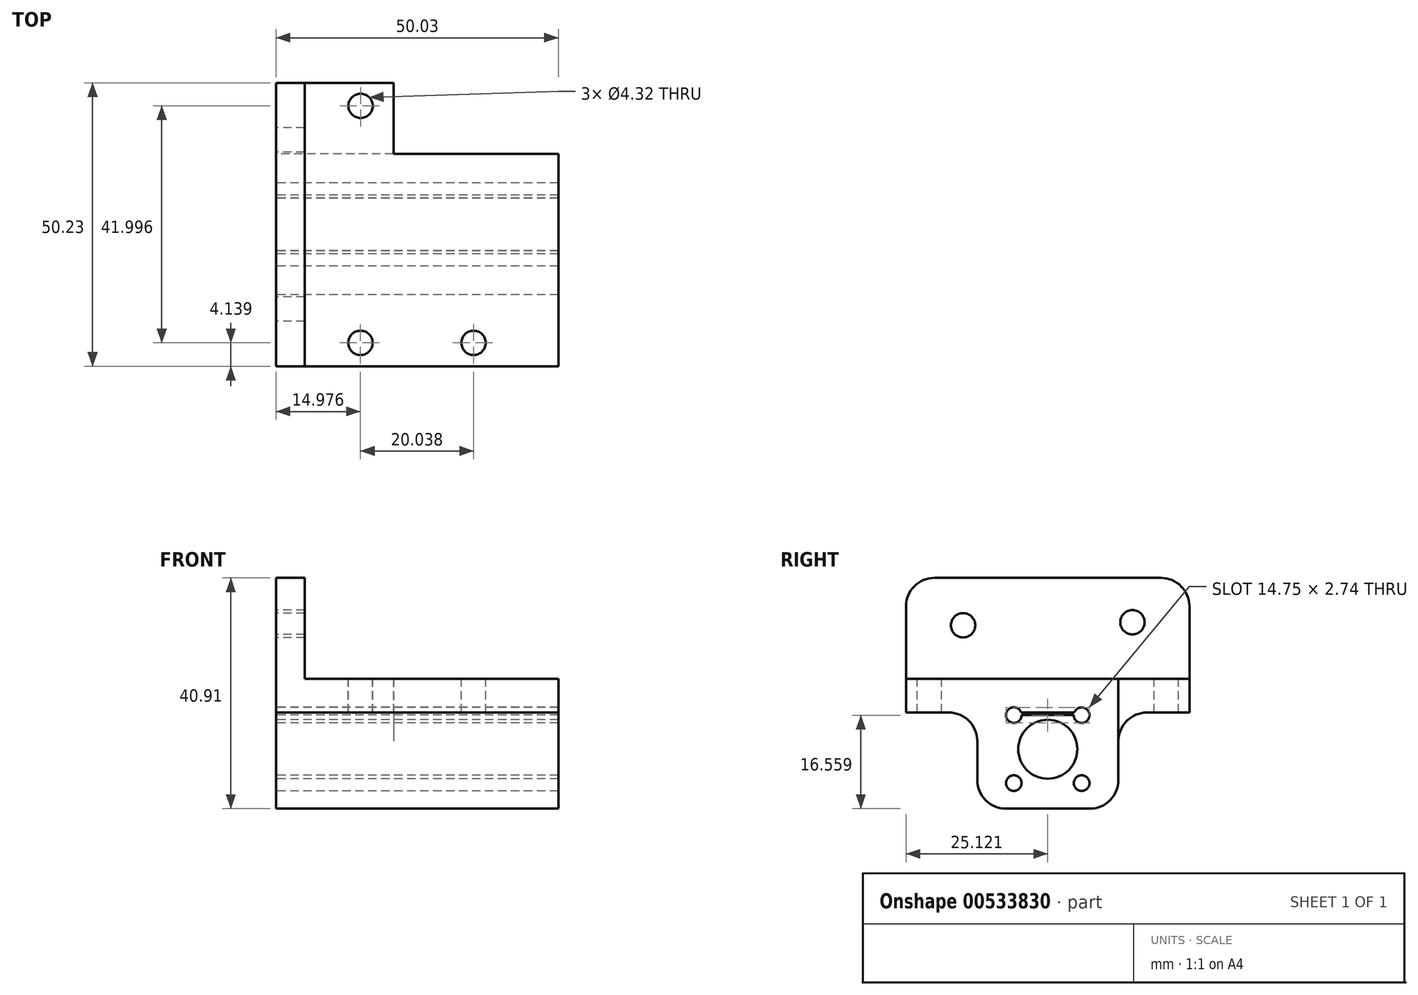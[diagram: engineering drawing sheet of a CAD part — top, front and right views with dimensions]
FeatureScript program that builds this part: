
annotation { "Feature Type Name" : "Feature", "Feature Type Description" : "" }
export const myFeature = defineFeature(function(context is Context, id is Id, definition is map)
    precondition{}
    {
        {
            var Q0;
            Q0=qCreatedBy(makeId("Right.planeOp"),FACE);
            cPlane(context, id + "F0", {"entities" : qUnion([Q0]), "cplaneType" : CPlaneType.OFFSET, "offset" : 25 * mm, "oppositeDirection" : true, "width" : 152.4 * mm, "height" : 152.4 * mm});
        }
        {
            var Q0;
            Q0=qCreatedBy(id+"F0.planeOp",FACE);
            var sketch = newSketch(context, id + "F1", { "sketchPlane" : qUnion([Q0])});
            skLineSegment(sketch, "E0.bottom", {"start": v(25.1, -3.49) * mm, "end": v(-25.13, -3.49) * mm});
            skLineSegment(sketch, "E0.top", {"start": v(25.1, 20.38) * mm, "end": v(-25.13, 20.38) * mm});
            skLineSegment(sketch, "E0.left", {"start": v(25.1, -3.49) * mm, "end": v(25.1, 20.38) * mm});
            skLineSegment(sketch, "E0.right", {"start": v(-25.13, -3.49) * mm, "end": v(-25.13, 20.38) * mm});
            skLineSegment(sketch, "E1.bottom", {"start": v(12.51, -3.49) * mm, "end": v(-12.48, -3.49) * mm});
            skLineSegment(sketch, "E1.top", {"start": v(12.51, -20.53) * mm, "end": v(-12.48, -20.53) * mm});
            skLineSegment(sketch, "E1.left", {"start": v(12.51, -3.49) * mm, "end": v(12.51, -20.53) * mm});
            skLineSegment(sketch, "E1.right", {"start": v(-12.48, -3.49) * mm, "end": v(-12.48, -20.53) * mm});
            skCircle(sketch, "E2", {"center": v(15, 12.5) * mm, "radius": 2 * mm});
            skCircle(sketch, "E3", {"center": v(-15, 11.97) * mm, "radius": 2 * mm});
            skCircle(sketch, "E4", {"center": v(0, -10) * mm, "radius": 5.23 * mm});
            skCircle(sketch, "E5", {"center": v(-6.02, -3.94) * mm, "radius": 1.39 * mm});
            skCircle(sketch, "E6", {"center": v(6, -3.96) * mm, "radius": 1.39 * mm});
            skLineSegment(sketch, "E7.bottom", {"start": v(6, -3.96) * mm, "end": v(-6.01, -3.96) * mm});
            skLineSegment(sketch, "E7.top", {"start": v(6, -16) * mm, "end": v(-6.01, -16) * mm});
            skLineSegment(sketch, "E7.left", {"start": v(6, -3.96) * mm, "end": v(6, -16) * mm});
            skLineSegment(sketch, "E7.right", {"start": v(-6.01, -3.96) * mm, "end": v(-6.01, -16) * mm});
            skCircle(sketch, "E8", {"center": v(6, -16) * mm, "radius": 1.39 * mm});
            skCircle(sketch, "E9", {"center": v(-6.01, -16) * mm, "radius": 1.39 * mm});
            skSolve(sketch);
        }
        {
            var Q0;
            {var subQ0=sQuery(id+"F1.wireOp",EDGE,"E6");var subQ1=sQuery(id+"F1.wireOp",EDGE,"E1.bottom");var subQ2=makeQuery(id+"F1.imprint","INTERSECT",VERTEX,{"disambiguationData":[OD(1.0)],"derivedFrom":[subQ1,subQ0]});Q0=makeQuery(id+"F1.imprint","IMPRINT",FACE,{"disambiguationData":[TD([[makeQuery(id+"F1.imprint","IMPRINT",EDGE,{"disambiguationData":[TD([[subQ2,-1.0]])],"derivedFrom":subQ1}),1.0]])]});}
            var Q1;
            Q1=makeQuery(id+"F1.imprint","IMPRINT",FACE,{"disambiguationData":[TD([[makeQuery(id+"F1.imprint","IMPRINT",EDGE,{"derivedFrom":sQuery(id+"F1.wireOp",EDGE,"E4")}),-1.0]])]});
            var Q2;
            Q2=makeQuery(id+"F1.imprint","IMPRINT",FACE,{"disambiguationData":[TD([[makeQuery(id+"F1.imprint","IMPRINT",EDGE,{"derivedFrom":sQuery(id+"F1.wireOp",EDGE,"E0.top")}),1.0]])]});
            var Q3;
            Q3=makeQuery(id+"F1.imprint","IMPRINT",FACE,{"disambiguationData":[TD([[makeQuery(id+"F1.imprint","IMPRINT",EDGE,{"derivedFrom":sQuery(id+"F1.wireOp",EDGE,"E1.top")}),-1.0]])]});
            extrude(context, id + "F2", {"entities" : qUnion([Q0, Q1, Q2, Q3]), "depth" : 5.08 * mm, "offsetDistance" : 25.4 * mm});
        }
        {
            var Q0;
            Q0=makeQuery(id+"F2.opExtrude","CAP_FACE",FACE,{"disambiguationData":[OSD([sQuery(id+"F1.wireOp",EDGE,"E0.bottom"),sQuery(id+"F1.wireOp",EDGE,"E0.top"),sQuery(id+"F1.wireOp",EDGE,"E0.left"),sQuery(id+"F1.wireOp",EDGE,"E0.right"),sQuery(id+"F1.wireOp",EDGE,"E1.top"),sQuery(id+"F1.wireOp",EDGE,"E1.left"),sQuery(id+"F1.wireOp",EDGE,"E1.right"),sQuery(id+"F1.wireOp",EDGE,"E2"),sQuery(id+"F1.wireOp",EDGE,"E3"),sQuery(id+"F1.wireOp",EDGE,"E4"),sQuery(id+"F1.wireOp",EDGE,"E5"),sQuery(id+"F1.wireOp",EDGE,"E6"),sQuery(id+"F1.wireOp",EDGE,"E8"),sQuery(id+"F1.wireOp",EDGE,"E9")])],"isStart":false});
            var sketch = newSketch(context, id + "F3", { "sketchPlane" : qUnion([Q0])});
            skLineSegment(sketch, "E10", {"start": v(-25.13, 2.5) * mm, "end": v(25.1, 2.5) * mm});
            skSolve(sketch);
        }
        {
            var Q0;
            {var subQ2=sQuery(id+"F3.wireOp",EDGE,"E10");Q0=makeQuery(id+"F3.imprint","IMPRINT",FACE,{"disambiguationData":[TD([[makeQuery(id+"F3.imprint","IMPRINT",EDGE,{"derivedFrom":subQ2}),-1.0]])]});}
            extrude(context, id + "F4", {"entities" : qUnion([Q0]), "operationType" : NewBodyOperationType.ADD, "depth" : 15.75 * mm, "offsetDistance" : 25.4 * mm});
        }
        {
            var Q0;
            Q0=makeQuery(id+"F4.opExtrude","CAP_FACE",FACE,{"disambiguationData":[OSD([sQuery(id+"F1.wireOp",EDGE,"E0.bottom"),sQuery(id+"F1.wireOp",EDGE,"E0.left"),sQuery(id+"F1.wireOp",EDGE,"E0.right"),sQuery(id+"F1.wireOp",EDGE,"E1.top"),sQuery(id+"F1.wireOp",EDGE,"E1.left"),sQuery(id+"F1.wireOp",EDGE,"E1.right"),sQuery(id+"F1.wireOp",EDGE,"E4"),sQuery(id+"F1.wireOp",EDGE,"E5"),sQuery(id+"F1.wireOp",EDGE,"E6"),sQuery(id+"F1.wireOp",EDGE,"E8"),sQuery(id+"F1.wireOp",EDGE,"E9"),sQuery(id+"F3.wireOp",EDGE,"E10")])],"isStart":false});
            var sketch = newSketch(context, id + "F5", { "sketchPlane" : qUnion([Q0])});
            skLineSegment(sketch, "E11", {"start": v(12.51, -3.49) * mm, "end": v(12.51, 2.5) * mm});
            skSolve(sketch);
        }
        {
            var Q0;
            {var subQ1=sQuery(id+"F5.wireOp",EDGE,"E11");Q0=makeQuery(id+"F5.imprint","IMPRINT",FACE,{"disambiguationData":[TD([[makeQuery(id+"F5.imprint","IMPRINT",EDGE,{"derivedFrom":subQ1}),1.0]])]});}
            extrude(context, id + "F6", {"entities" : qUnion([Q0]), "operationType" : NewBodyOperationType.ADD, "depth" : 29.2 * mm, "offsetDistance" : 25.4 * mm});
        }
        {
            var Q0;
            {var subQ0=sQuery(id+"F3.wireOp",EDGE,"E10");Q0=makeQuery(id+"F6.boolean.opBoolean","MERGE",FACE,{"derivedFrom":[makeQuery(id+"F4.opExtrude","SWEPT_FACE",FACE,{"disambiguationData":[OSD([subQ0])]}),makeQuery(id+"F6.opExtrude","SWEPT_FACE",FACE,{"disambiguationData":[OSD([subQ0])]})]});}
            var sketch = newSketch(context, id + "F7", { "sketchPlane" : qUnion([Q0])});
            skCircle(sketch, "E12", {"center": v(-10, 21) * mm, "radius": 2.01 * mm});
            skCircle(sketch, "E13", {"center": v(-10.01, -20.99) * mm, "radius": 2.01 * mm});
            skCircle(sketch, "E14", {"center": v(10.02, -21) * mm, "radius": 2.01 * mm});
            skSolve(sketch);
        }
        {
            var Q0;
            Q0 = qSketchRegion(id + "F7", true);
            extrude(context, id + "F8", {"entities" : qUnion([Q0]), "operationType" : NewBodyOperationType.REMOVE, "oppositeDirection" : true, "depth" : 25.4 * mm, "offsetDistance" : 25.4 * mm});
        }
        {
            var Q0;
            {var subQ0=sQuery(id+"F1.wireOp",EDGE,"E1.right");var subQ1=sQuery(id+"F1.wireOp",EDGE,"E1.top");Q0=makeQuery(id+"F6.boolean.opBoolean","MERGE",EDGE,{"derivedFrom":[makeQuery(id+"F4.boolean.opBoolean","MERGE",EDGE,{"derivedFrom":[makeQuery(id+"F2.opExtrude","SWEPT_EDGE",EDGE,{"disambiguationData":[OSD([subQ1,subQ0])]}),makeQuery(id+"F4.opExtrude","SWEPT_EDGE",EDGE,{"disambiguationData":[OSD([subQ1,subQ0])]})]}),makeQuery(id+"F6.opExtrude","SWEPT_EDGE",EDGE,{"disambiguationData":[OSD([subQ1,subQ0])]})]});}
            var Q1;
            {var subQ0=sQuery(id+"F1.wireOp",EDGE,"E1.left");var subQ1=sQuery(id+"F1.wireOp",EDGE,"E1.top");Q1=makeQuery(id+"F6.boolean.opBoolean","MERGE",EDGE,{"derivedFrom":[makeQuery(id+"F4.boolean.opBoolean","MERGE",EDGE,{"derivedFrom":[makeQuery(id+"F2.opExtrude","SWEPT_EDGE",EDGE,{"disambiguationData":[OSD([subQ1,subQ0])]}),makeQuery(id+"F4.opExtrude","SWEPT_EDGE",EDGE,{"disambiguationData":[OSD([subQ1,subQ0])]})]}),makeQuery(id+"F6.opExtrude","SWEPT_EDGE",EDGE,{"disambiguationData":[OSD([subQ1,subQ0])]})]});}
            var Q2;
            {var subQ0=sQuery(id+"F1.wireOp",EDGE,"E1.right");var subQ1=sQuery(id+"F1.wireOp",EDGE,"E0.bottom");Q2=makeQuery(id+"F6.boolean.opBoolean","MERGE",EDGE,{"derivedFrom":[makeQuery(id+"F4.boolean.opBoolean","MERGE",EDGE,{"derivedFrom":[makeQuery(id+"F2.opExtrude","SWEPT_EDGE",EDGE,{"disambiguationData":[OSD([subQ1,sQuery(id+"F1.wireOp",EDGE,"E1.bottom"),subQ0])]}),makeQuery(id+"F4.opExtrude","SWEPT_EDGE",EDGE,{"disambiguationData":[OSD([subQ1,subQ0])]})]}),makeQuery(id+"F6.opExtrude","SWEPT_EDGE",EDGE,{"disambiguationData":[OSD([subQ1,subQ0])]})]});}
            var Q3;
            {var subQ0=sQuery(id+"F1.wireOp",EDGE,"E1.left");var subQ1=sQuery(id+"F1.wireOp",EDGE,"E0.bottom");Q3=makeQuery(id+"F4.boolean.opBoolean","MERGE",EDGE,{"derivedFrom":[makeQuery(id+"F2.opExtrude","SWEPT_EDGE",EDGE,{"disambiguationData":[OSD([subQ1,sQuery(id+"F1.wireOp",EDGE,"E1.bottom"),subQ0])]}),makeQuery(id+"F4.opExtrude","SWEPT_EDGE",EDGE,{"disambiguationData":[OSD([subQ1,subQ0])]})]});}
            var Q4;
            Q4=makeQuery(id+"F2.opExtrude","SWEPT_EDGE",EDGE,{"disambiguationData":[OSD([sQuery(id+"F1.wireOp",EDGE,"E0.top"),sQuery(id+"F1.wireOp",EDGE,"E0.right")])]});
            var Q5;
            Q5=makeQuery(id+"F2.opExtrude","SWEPT_EDGE",EDGE,{"disambiguationData":[OSD([sQuery(id+"F1.wireOp",EDGE,"E0.top"),sQuery(id+"F1.wireOp",EDGE,"E0.left")])]});
            fillet(context, id + "F9", {"entities" : qUnion([Q0, Q1, Q2, Q3, Q4, Q5]), "radius" : 5.08 * mm, "tangentPropagation" : true, "allowEdgeOverflow" : false});
        }
        {
            var Q0;
            Q0=makeQuery(id+"F2.opExtrude","CAP_FACE",FACE,{"disambiguationData":[OSD([sQuery(id+"F1.wireOp",EDGE,"E0.bottom"),sQuery(id+"F1.wireOp",EDGE,"E0.top"),sQuery(id+"F1.wireOp",EDGE,"E0.left"),sQuery(id+"F1.wireOp",EDGE,"E0.right"),sQuery(id+"F1.wireOp",EDGE,"E1.top"),sQuery(id+"F1.wireOp",EDGE,"E1.left"),sQuery(id+"F1.wireOp",EDGE,"E1.right"),sQuery(id+"F1.wireOp",EDGE,"E2"),sQuery(id+"F1.wireOp",EDGE,"E3"),sQuery(id+"F1.wireOp",EDGE,"E4"),sQuery(id+"F1.wireOp",EDGE,"E5"),sQuery(id+"F1.wireOp",EDGE,"E6"),sQuery(id+"F1.wireOp",EDGE,"E8"),sQuery(id+"F1.wireOp",EDGE,"E9")])],"isStart":true});
            var sketch = newSketch(context, id + "F10", { "sketchPlane" : qUnion([Q0])});
            skCircle(sketch, "E15", {"center": v(-15, 12.5) * mm, "radius": 2.16 * mm});
            skCircle(sketch, "E16", {"center": v(15, 11.97) * mm, "radius": 2.16 * mm});
            skSolve(sketch);
        }
        {
            var Q0;
            Q0 = qSketchRegion(id + "F10", true);
            extrude(context, id + "F11", {"entities" : qUnion([Q0]), "operationType" : NewBodyOperationType.REMOVE, "oppositeDirection" : true, "depth" : 25.4 * mm, "offsetDistance" : 25.4 * mm});
        }
        {
            var Q0;
            {var subQ0=sQuery(id+"F3.wireOp",EDGE,"E10");Q0=makeQuery(id+"F6.boolean.opBoolean","MERGE",FACE,{"derivedFrom":[makeQuery(id+"F4.opExtrude","SWEPT_FACE",FACE,{"disambiguationData":[OSD([subQ0])]}),makeQuery(id+"F6.opExtrude","SWEPT_FACE",FACE,{"disambiguationData":[OSD([subQ0])]})]});}
            var sketch = newSketch(context, id + "F12", { "sketchPlane" : qUnion([Q0])});
            skCircle(sketch, "E17", {"center": v(-10, 21) * mm, "radius": 2.16 * mm});
            skCircle(sketch, "E18", {"center": v(-10.01, -20.99) * mm, "radius": 2.16 * mm});
            skCircle(sketch, "E19", {"center": v(10.02, -21) * mm, "radius": 2.16 * mm});
            skSolve(sketch);
        }
        {
            var Q0;
            Q0 = qSketchRegion(id + "F12", true);
            extrude(context, id + "F13", {"entities" : qUnion([Q0]), "operationType" : NewBodyOperationType.REMOVE, "oppositeDirection" : true, "depth" : 25.4 * mm, "offsetDistance" : 25.4 * mm});
        }
    });
